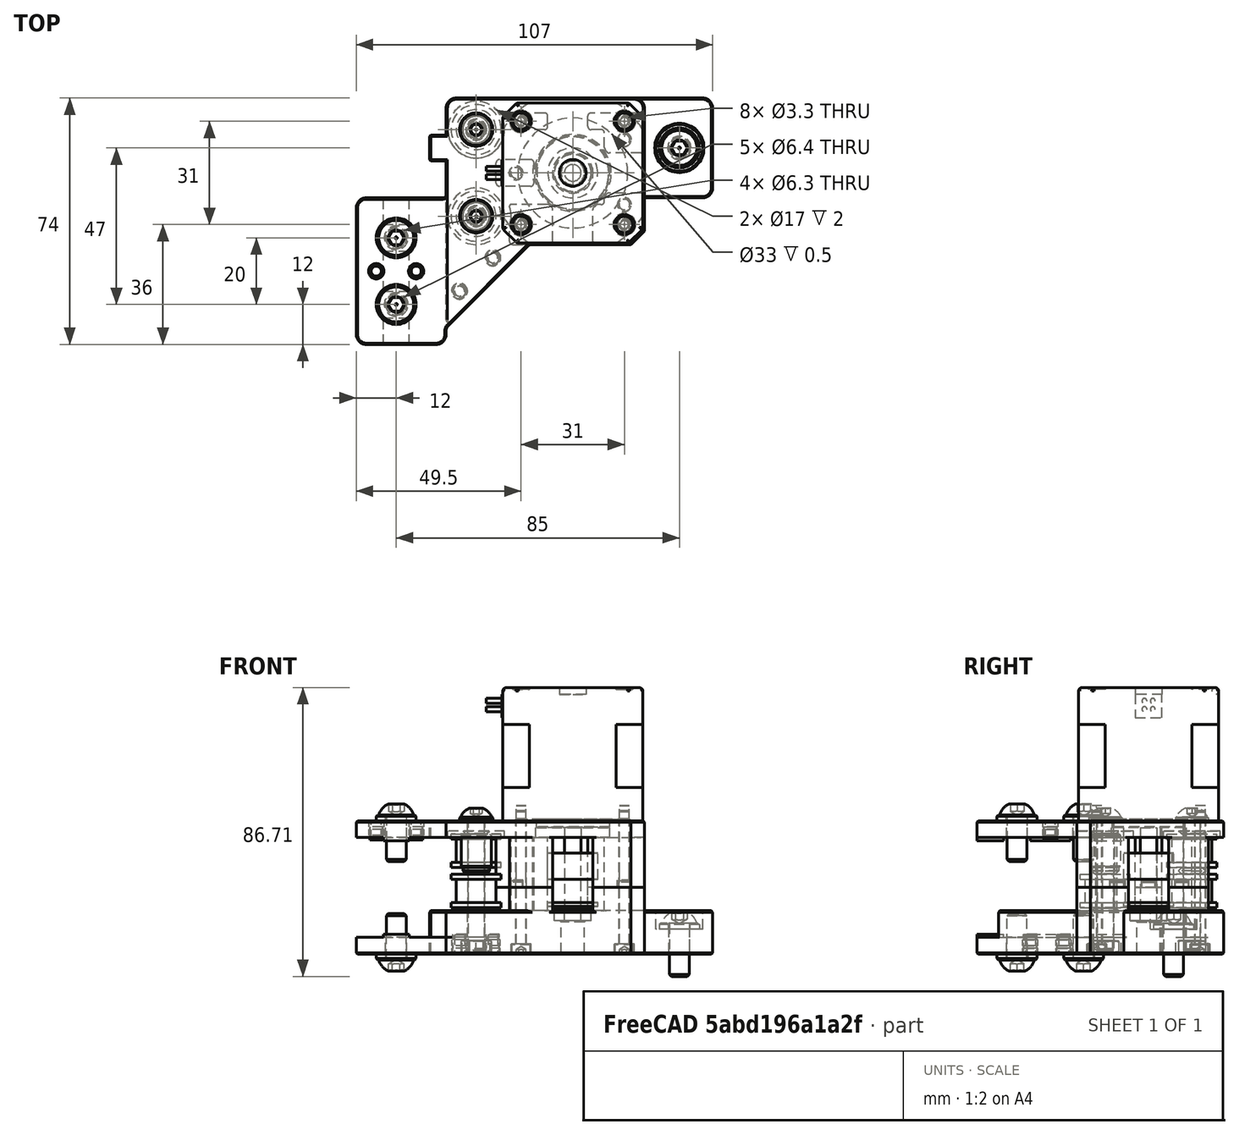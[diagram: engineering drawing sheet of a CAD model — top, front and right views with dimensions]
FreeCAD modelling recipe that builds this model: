
FCSTD DOCUMENT  (FreeCAD 0.19R24366 (Git))
Label: ab-x-motor-assembly
License: Other
LicenseURL: GPL3
objects: Part::FeaturePython×24, Part::Feature×10, Spreadsheet::Sheet×2, PartDesign::CoordinateSystem×1, App::Part×1
note: 35 computed .brp shape members not serialized (recipe doc carries the construction recipe); baked Part::Feature solids carry a one-line shape summary decoded from their .brp

FEATURE [Part::Feature] Cut002007  label="smooth-idler-6mm006"
  Placement = pos=(9,-35.5,9) rot=(0,0,-1;1.5708rad)
  shape: bbox 15 x 15 x 10 mm, 8 faces (baked)
FEATURE [Part::Feature] Cut002005  label="smooth-idler-6mm004"
  Placement = pos=(9,-9.5,9) rot=(0,0,-1;1.5708rad)
  shape: bbox 15 x 15 x 10 mm, 8 faces (baked)
FEATURE [Part::Feature] Cut001  label="smooth-idler-6mm"
  Placement = pos=(9,-9.5,21) rot=(0,0,-1;1.5708rad)
  shape: bbox 15 x 15 x 10 mm, 8 faces (baked)
FEATURE [Part::Feature] Cut002008017  label="ab-motor-idler-spacer"
  Placement = pos=(9,-35.5,31) rot=(0,1,0;3.14159rad)
  shape: bbox 9 x 9 x 11.85 mm, 9 faces (baked)
FEATURE [Part::Feature] Cut002001  label="20t-pulley001"
  Placement = pos=(38,-22.5,9.3) rot=(0,0,1;0rad)
  shape: bbox 15 x 15 x 16 mm, 8 faces (baked)
FEATURE [Part::Feature] Fusion006002011004053036004001001  label="motor-40mm"
  Placement = pos=(38,-22.5,75) rot=(0.707107,0.707107,0;3.14159rad)
  shape: bbox 47 x 42 x 67 mm, 100 faces (baked)
FEATURE [Part::Feature] Cut002008018  label="MR115ZZ"
  Placement = pos=(38,-22.5,5) rot=(0,0,1;0rad)
  shape: bbox 11 x 11 x 4 mm, 4 faces (baked)
FEATURE [Part::Feature] Cut002008019  label="motor-mount-stack-idler-spacer"
  Placement = pos=(9,-9.5,20) rot=(0,0,1;0rad)
  shape: bbox 8 x 8 x 1.7 mm, 5 faces (baked)
FEATURE [Part::FeaturePython] Washer  label="M6-Washer"  # Fasteners workbench fastener (typed FeaturePython)
  Placement = pos=(-15,-42,35) rot=(0,0,1;0rad)
  diameter = 2
  invert = false
  matchOuter = true
  offset = 0
  type = 4
FEATURE [Part::FeaturePython] Washer001  label="M6-Washer007"  # Fasteners workbench fastener (typed FeaturePython)
  Placement = pos=(-15,-62,35) rot=(0,0,1;0rad)
  diameter = 2
  invert = false
  matchOuter = true
  offset = 0
  type = 4
FEATURE [Part::FeaturePython] Washer002  label="M6-Washer008"  # Fasteners workbench fastener (typed FeaturePython)
  Placement = pos=(-15,-42,-5) rot=(1,0,0;3.14159rad)
  diameter = 2
  invert = true
  matchOuter = true
  offset = 0
  type = 4
FEATURE [Part::FeaturePython] Washer003  label="M6-Washer009"  # Fasteners workbench fastener (typed FeaturePython)
  Placement = pos=(-15,-62,-5) rot=(1,0,0;3.14159rad)
  diameter = 2
  invert = true
  matchOuter = true
  offset = 0
  type = 4
FEATURE [Part::FeaturePython] Washer004  label="M6-Washer010"  # Fasteners workbench fastener (typed FeaturePython)
  Placement = pos=(70,-15,2.5) rot=(0,0,1;0rad)
  diameter = 2
  invert = false
  matchOuter = true
  offset = 0
  type = 4
FEATURE [Part::FeaturePython] Nut  label="M5-Nut"  # Fasteners workbench fastener (typed FeaturePython)
  Placement = pos=(9,-9.5,-1) rot=(1,0,0;3.14159rad)
  diameter = 7
  invert = true
  leftHanded = false
  matchOuter = true
  offset = 0
  thread = false
  type = 7
FEATURE [Part::FeaturePython] Nut001  label="M5-Nut001"  # Fasteners workbench fastener (typed FeaturePython)
  Placement = pos=(9,-35.5,-1) rot=(1,0,0;3.14159rad)
  diameter = 7
  invert = true
  leftHanded = false
  matchOuter = true
  offset = 0
  thread = false
  type = 7
FEATURE [Part::FeaturePython] Screw  label="M3x40-Screw"  # Fasteners workbench fastener (typed FeaturePython)
  Placement = pos=(53.5,-7,-2) rot=(1,0,0;3.14159rad)
  diameter = 4
  invert = true
  leftHanded = false
  length = 10
  lengthCustom = 40
  matchOuter = true
  offset = 0
  thread = false
  type = 33
FEATURE [Part::FeaturePython] Screw001  label="M3x40-Screw007"  # Fasteners workbench fastener (typed FeaturePython)
  Placement = pos=(22.5,-7,-2) rot=(1,0,0;3.14159rad)
  diameter = 4
  invert = true
  leftHanded = false
  length = 10
  lengthCustom = 40
  matchOuter = true
  offset = 0
  thread = false
  type = 33
FEATURE [Part::FeaturePython] Screw002  label="M3x40-Screw008"  # Fasteners workbench fastener (typed FeaturePython)
  Placement = pos=(22.5,-38,-2) rot=(1,0,0;3.14159rad)
  diameter = 4
  invert = true
  leftHanded = false
  length = 10
  lengthCustom = 40
  matchOuter = true
  offset = 0
  thread = false
  type = 33
FEATURE [Part::FeaturePython] Screw003  label="M3x40-Screw006"  # Fasteners workbench fastener (typed FeaturePython)
  Placement = pos=(53.5,-38,-2) rot=(1,0,0;3.14159rad)
  diameter = 4
  invert = true
  leftHanded = false
  length = 10
  lengthCustom = 40
  matchOuter = true
  offset = 0
  thread = false
  type = 33
FEATURE [Part::FeaturePython] Screw004  label="M6x16-Screw"  # Fasteners workbench fastener (typed FeaturePython)
  Placement = pos=(70,-15,4.3) rot=(0,0,1;0rad)
  baseObject = -> Washer004 [Edge1]
  diameter = 4
  invert = false
  leftHanded = false
  length = 3
  lengthCustom = 16
  matchOuter = true
  offset = 0
  thread = false
  type = 39
FEATURE [Part::FeaturePython] Screw005  label="M6x14-Screw"  # Fasteners workbench fastener (typed FeaturePython)
  Placement = pos=(-15,-42,36.8) rot=(0,0,1;0rad)
  baseObject = -> Washer [Edge1]
  diameter = 4
  invert = false
  leftHanded = false
  length = 2
  lengthCustom = 14
  matchOuter = true
  offset = 0
  thread = false
  type = 39
FEATURE [Part::FeaturePython] Screw006  label="M6x14-Screw001"  # Fasteners workbench fastener (typed FeaturePython)
  Placement = pos=(-15,-62,36.8) rot=(0,0,1;0rad)
  baseObject = -> Washer001 [Edge1]
  diameter = 4
  invert = false
  leftHanded = false
  length = 2
  lengthCustom = 14
  matchOuter = true
  offset = 0
  thread = false
  type = 39
FEATURE [Part::FeaturePython] Screw007  label="M6x14-Screw002"  # Fasteners workbench fastener (typed FeaturePython)
  Placement = pos=(-15,-62,-6.8) rot=(1,0,0;3.14159rad)
  baseObject = -> Washer003 [Edge1]
  diameter = 4
  invert = false
  leftHanded = false
  length = 2
  lengthCustom = 14
  matchOuter = true
  offset = 0
  thread = false
  type = 39
FEATURE [Part::FeaturePython] Screw008  label="M6x14-Screw003"  # Fasteners workbench fastener (typed FeaturePython)
  Placement = pos=(-15,-42,-6.8) rot=(1,0,0;3.14159rad)
  baseObject = -> Washer002 [Edge1]
  diameter = 4
  invert = false
  leftHanded = false
  length = 2
  lengthCustom = 14
  matchOuter = true
  offset = 0
  thread = false
  type = 39
FEATURE [PartDesign::CoordinateSystem] LCS_ab_x_motor  label="LCS_ab-x-motor"
  AttacherType = Attacher::AttachEngine3D
FEATURE [Part::FeaturePython] HeatSet  label="M3x4-HeatSet"  # WARN: FeaturePython — macro-defined, semantics opaque (R4)
  Placement = pos=(-21,-52,35) rot=(0,0,1;0rad)
  diameter = 2
  invert = false
  offset = 0
FEATURE [Part::FeaturePython] HeatSet001  label="M3x4-HeatSet001"  # WARN: FeaturePython — macro-defined, semantics opaque (R4)
  Placement = pos=(-9,-52,35) rot=(0,0,1;0rad)
  diameter = 2
  invert = false
  offset = 0
FEATURE [Part::FeaturePython] HeatSet002  label="M3x4-HeatSet002"  # WARN: FeaturePython — macro-defined, semantics opaque (R4)
  Placement = pos=(4,-58,-5) rot=(1,0,0;3.14159rad)
  diameter = 2
  invert = true
  offset = 0
FEATURE [Part::FeaturePython] HeatSet003  label="M3x4-HeatSet003"  # WARN: FeaturePython — macro-defined, semantics opaque (R4)
  Placement = pos=(14,-48,-5) rot=(1,0,0;3.14159rad)
  diameter = 2
  invert = true
  offset = 0
FEATURE [Part::FeaturePython] Washer005  label="M5-Washer"  # Fasteners workbench fastener (typed FeaturePython)
  Placement = pos=(9,-9.5,35) rot=(0,0,1;0rad)
  diameter = 1
  invert = false
  matchOuter = true
  offset = 0
  type = 4
FEATURE [Part::FeaturePython] Washer006  label="M5-Washer001"  # Fasteners workbench fastener (typed FeaturePython)
  Placement = pos=(9,-35.5,35) rot=(0,0,1;0rad)
  diameter = 1
  invert = false
  matchOuter = true
  offset = 0
  type = 4
FEATURE [Part::FeaturePython] Screw009  label="M5x40-Screw"  # Fasteners workbench fastener (typed FeaturePython)
  Placement = pos=(9,-9.5,36.1) rot=(0,0,1;0rad)
  baseObject = -> Washer005 [Edge1]
  diameter = 3
  invert = false
  leftHanded = false
  length = 9
  lengthCustom = 40
  matchOuter = true
  offset = 0
  thread = false
  type = 40
FEATURE [Part::FeaturePython] Screw010  label="M5x40-Screw001"  # Fasteners workbench fastener (typed FeaturePython)
  Placement = pos=(9,-35.5,36.1) rot=(0,0,1;0rad)
  baseObject = -> Washer006 [Edge1]
  diameter = 3
  invert = false
  leftHanded = false
  length = 9
  lengthCustom = 40
  matchOuter = true
  offset = 0
  thread = false
  type = 40
FEATURE [Spreadsheet::Sheet] Fasteners_BOM
  cells = A1=Type; B1=Qty; A2=Heat Set Insert M3; B2=8; A3=ISO4032 Nut M5; B3=4; A4=ISO4762 Screw M3x40; B4=8; A5=ISO7090 Washer M5; B5=8; A6=ISO7090 Washer M6; B6=20; A7=ISO7380-1 Screw M5x40; B7=4; A8=ISO7380-1 Screw M6x14; B8=8; A9=ISO7380-1 Screw M6x16; B9=2
FEATURE [Spreadsheet::Sheet] Fasteners_BOM001
  cells = A1=Type; B1=Qty; A2=Heat Set Insert M3; B2=8; A3=ISO4032 Nut M5; B3=4; A4=ISO4762 Screw M3x40; B4=8; A5=ISO7090 Washer M5; B5=8; A6=ISO7090 Washer M6; B6=20; A7=ISO7380-1 Screw M5x40; B7=4; A8=ISO7380-1 Screw M6x14; B8=8; A9=ISO7380-1 Screw M6x16; B9=2
FEATURE [Part::Feature] Chamfer043001  label="ab-motor-bottom-left"
  Placement = pos=(0,-30,0) rot=(0,0,1;0rad)
  shape: bbox 107 x 74 x 22 mm, 227 faces (baked)
FEATURE [Part::Feature] Chamfer044001  label="ab-motor-top-left"
  Placement = pos=(0,-30,0) rot=(0,0,1;0rad)
  shape: bbox 86.5 x 74 x 20 mm, 159 faces (baked)
FEATURE [App::Part] Part  label="ab-x-motor"
  Group = -> [Cut002008017,Cut001,Cut002007,Cut002005,Fusion006002011004053036004001001,Cut002001,Cut002008018,Cut002008019,Screw003,Washer004,Washer,Washer002,Washer001,Washer003,Screw008,Screw007,Screw006,Screw005,Screw004,Screw002,Screw001,Screw,Nut001,Nut,LCS_ab_x_motor,HeatSet,HeatSet001,HeatSet002,HeatSet003,Washer005,Washer006,Screw009,Screw010,Chamfer044001,Chamfer043001]
  Origin = -> Origin
